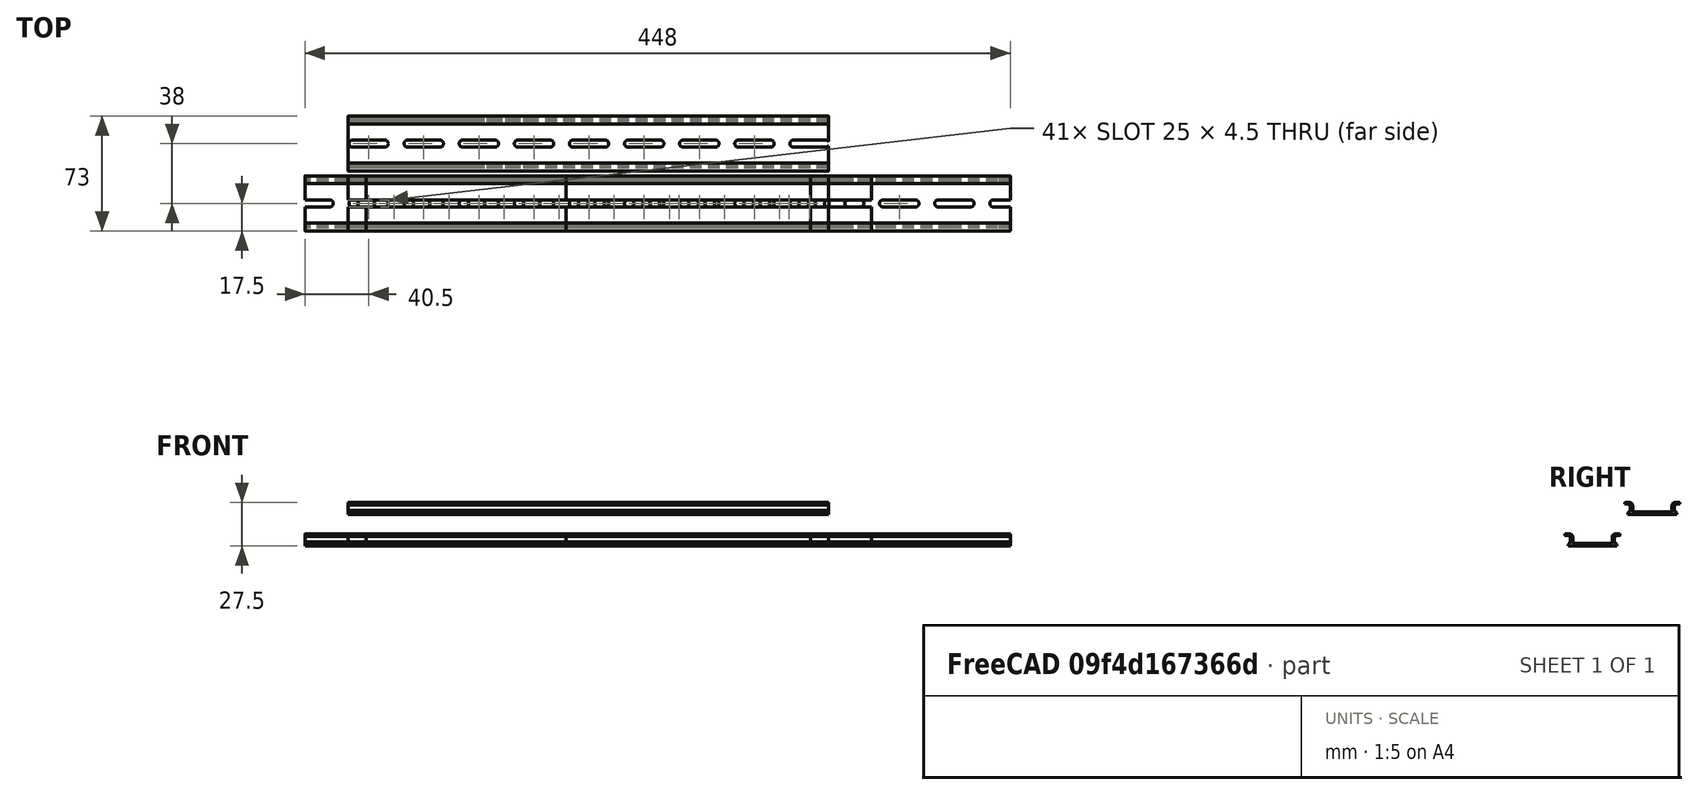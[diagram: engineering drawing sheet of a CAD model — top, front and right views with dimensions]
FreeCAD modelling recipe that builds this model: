
FCSTD DOCUMENT  (FreeCAD 0.18R16146 (Git))
Label: din-rail
License: Other
LicenseURL: GPL3
objects: Part::Feature×12, Part::Cylinder×4, Part::Cut×4, Part::MultiFuse×2, Part::Box×2, Part::MultiCommon×2
note: 26 computed .brp shape members not serialized (recipe doc carries the construction recipe); baked Part::Feature solids carry a one-line shape summary decoded from their .brp

FEATURE [Part::Feature] Part__Feature  label="_DNR314-100"
  shape: bbox 100 x 35 x 7.5 mm, 42 faces (baked)
FEATURE [Part::Feature] Part__Feature001  label="_DNR314-101"
  Placement = pos=(140,0,0) rot=(0,0,1;0rad)
  shape: bbox 100 x 35 x 7.5 mm, 42 faces (baked)
FEATURE [Part::Feature] Part__Feature002  label="_DNR314-102"
  Placement = pos=(70,0,0) rot=(0,0,1;0rad)
  shape: bbox 100 x 35 x 7.5 mm, 42 faces (baked)
FEATURE [Part::Feature] Part__Feature003  label="_DNR314-103"
  Placement = pos=(210,0,0) rot=(0,0,1;0rad)
  shape: bbox 100 x 35 x 7.5 mm, 42 faces (baked)
FEATURE [Part::Feature] Part__Feature004  label="_DNR314-104"
  Placement = pos=(280,0,0) rot=(0,0,1;0rad)
  shape: bbox 100 x 35 x 7.5 mm, 42 faces (baked)
FEATURE [Part::Cylinder] Cylinder
  Angle = 360
  AttacherType = Attacher::AttachEngine3D
  Height = 10
  Placement = pos=(48,0,0) rot=(0,0,1;0rad)
  Radius = 5
FEATURE [Part::Cylinder] Cylinder001
  Angle = 360
  AttacherType = Attacher::AttachEngine3D
  Height = 10
  Placement = pos=(118,0,0) rot=(0,0,1;0rad)
  Radius = 5
FEATURE [Part::Cylinder] Cylinder002
  Angle = 360
  AttacherType = Attacher::AttachEngine3D
  Height = 10
  Placement = pos=(188,0,0) rot=(0,0,1;0rad)
  Radius = 5
FEATURE [Part::Cylinder] Cylinder003
  Angle = 360
  AttacherType = Attacher::AttachEngine3D
  Height = 10
  Placement = pos=(259,0,0) rot=(0,0,1;0rad)
  Radius = 5
FEATURE [Part::Cut] Cut
  Base = -> Part__Feature003
  Tool = -> Cylinder003
FEATURE [Part::Cut] Cut001
  Base = -> Part__Feature001
  Tool = -> Cylinder002
FEATURE [Part::Cut] Cut002
  Base = -> Part__Feature002
  Tool = -> Cylinder001
FEATURE [Part::Cut] Cut003
  Base = -> Part__Feature
  Tool = -> Cylinder
FEATURE [Part::MultiFuse] Fusion
  Shapes = -> [Cut003,Cut002,Cut001,Cut,Part__Feature004]
FEATURE [Part::Box] Box  label="Cube"
  AttacherType = Attacher::AttachEngine3D
  Height = 10
  Length = 282
  Placement = pos=(-14,-21,0) rot=(0,0,1;0rad)
  Width = 44
FEATURE [Part::MultiCommon] Common
  Shapes = -> [Box,Fusion]
FEATURE [Part::Feature] Common001  label="din-282mm"
  Placement = pos=(-127,0,0) rot=(0,0,1;0rad)
  shape: bbox 282 x 35 x 7.5 mm, 66 faces (baked)
FEATURE [Part::Feature] Common001001  label="din-282mm001"
  shape: bbox 282 x 35 x 7.5 mm, 66 faces (baked)
FEATURE [Part::Feature] Common001002  label="din-282mm002"
  Placement = pos=(245,0,0) rot=(0,0,1;0rad)
  shape: bbox 282 x 35 x 7.5 mm, 66 faces (baked)
FEATURE [Part::MultiFuse] Fusion001
  Placement = pos=(-175,38,20) rot=(0,0,1;0rad)
  Shapes = -> [Common001001,Common001002]
FEATURE [Part::Feature] Common001003001  label="din-360mm"
  Placement = pos=(135,-20,-20) rot=(0,0,1;0rad)
  shape: bbox 360 x 35 x 7.5 mm, 74 faces (baked)
FEATURE [Part::Box] Box001  label="Cube001"
  AttacherType = Attacher::AttachEngine3D
  Height = 50
  Length = 305
  Placement = pos=(-152.5,17,0) rot=(0,0,1;0rad)
  Width = 50
FEATURE [Part::Feature] Common001003002001  label="din-305mm"
  Placement = pos=(0,-27,-20) rot=(0,0,1;0rad)
  shape: bbox 305 x 35 x 7.5 mm, 70 faces (baked)
FEATURE [Part::Feature] Common001003001001  label="din-360mm001"
  shape: bbox 360 x 35 x 7.5 mm, 74 faces (baked)
FEATURE [Part::MultiCommon] Common001003002002
  Shapes = -> [Fusion001,Box001]
FEATURE [Part::Feature] Common001003002002001  label="sin-309mm"
  shape: bbox 305 x 35 x 7.5 mm, 68 faces (baked)
